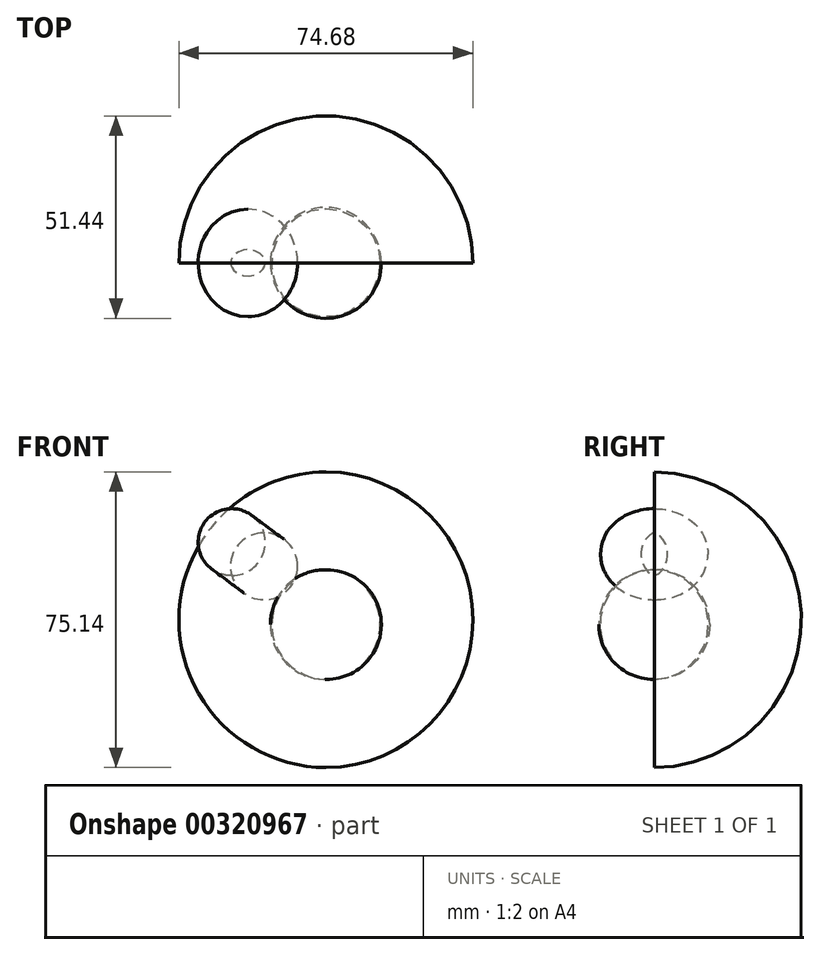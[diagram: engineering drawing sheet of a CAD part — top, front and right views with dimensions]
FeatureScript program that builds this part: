
annotation { "Feature Type Name" : "Feature", "Feature Type Description" : "" }
export const myFeature = defineFeature(function(context is Context, id is Id, definition is map)
    precondition{}
    {
        {
            var Q0;
            Q0=qCreatedBy(makeId("Front.planeOp"),FACE);
            var sketch = newSketch(context, id + "F0", { "sketchPlane" : qUnion([Q0])});
            skLineSegment(sketch, "E0", {"start": v(0, 0) * mm, "end": v(0, 75.14) * mm});
            skArc(sketch, "E1", {"start": v(0, 0) * mm, "mid": v(37.34, 37.57) * mm, "end": v(0, 75.14) * mm});
            skSolve(sketch);
        }
        {
            var Q0;
            Q0 = qSketchRegion(id + "F0", true);
            var Q1;
            Q1=sQuery(id+"F0.wireOp",EDGE,"E0");
            revolve(context, id + "F1", {"entities" : qUnion([Q0]), "axis" : qUnion([Q1]), "revolveType" : RevolveType.TWO_DIRECTIONS, "angle" : 180 * degree, "angleBack" : 0 * degree});
        }
        {
            var Q0;
            Q0 = qSketchRegion(id + "F0", true);
            var sketch = newSketch(context, id + "F2", { "sketchPlane" : qUnion([Q0])});
            skLineSegment(sketch, "E2", {"start": v(0, 22.42) * mm, "end": v(0, 50.28) * mm});
            skArc(sketch, "E3", {"start": v(0, 22.42) * mm, "mid": v(14.1, 36.35) * mm, "end": v(0, 50.28) * mm});
            skSolve(sketch);
        }
        {
            var Q0;
            Q0 = qSketchRegion(id + "F2", true);
            var Q1;
            Q1=sQuery(id+"F0.wireOp",EDGE,"E0");
            revolve(context, id + "F3", {"entities" : qUnion([Q0]), "axis" : qUnion([Q1]), "revolveType" : RevolveType.FULL});
        }
        {
            var Q0;
            Q0=qCreatedBy(makeId("Front.planeOp"),FACE);
            var sketch = newSketch(context, id + "F4", { "sketchPlane" : qUnion([Q0])});
            skLineSegment(sketch, "E4", {"start": v(-15.76, 59.67) * mm, "end": v(-23.87, 48.77) * mm});
            skArc(sketch, "E5", {"start": v(-23.87, 48.77) * mm, "mid": v(-17.1, 52.2) * mm, "end": v(-15.76, 59.67) * mm});
            skSolve(sketch);
        }
        {
            var Q0;
            Q0 = qSketchRegion(id + "F4", true);
            var Q1;
            Q1=sQuery(id+"F4.wireOp",EDGE,"E4");
            revolve(context, id + "F5", {"entities" : qUnion([Q0]), "axis" : qUnion([Q1]), "revolveType" : RevolveType.FULL});
        }
    });
